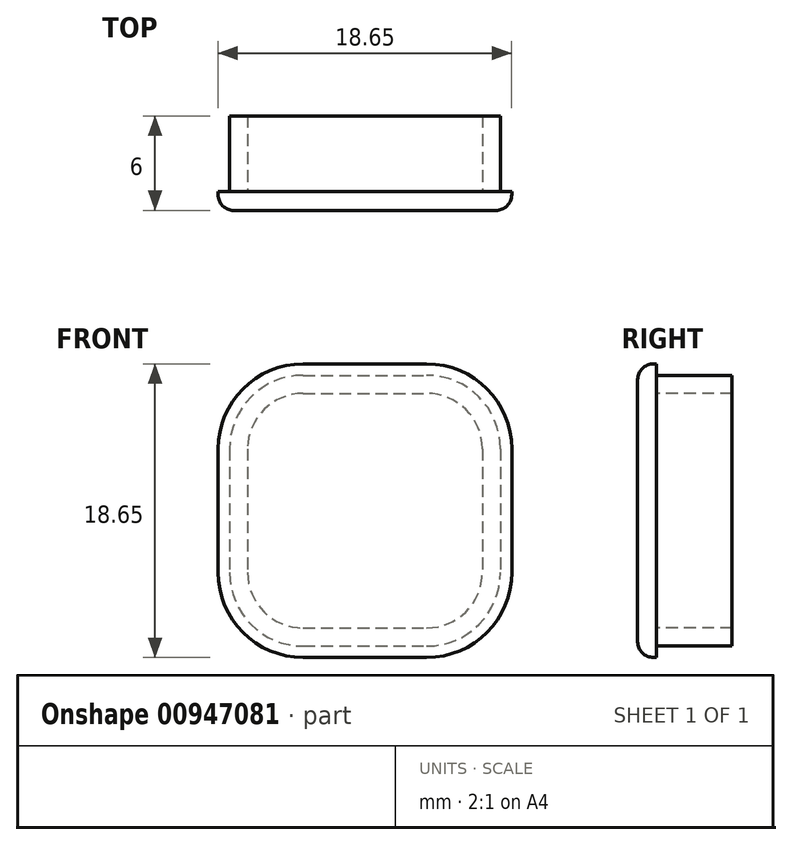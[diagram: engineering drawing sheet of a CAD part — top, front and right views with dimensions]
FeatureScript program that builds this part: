
annotation { "Feature Type Name" : "Feature", "Feature Type Description" : "" }
export const myFeature = defineFeature(function(context is Context, id is Id, definition is map)
    precondition{}
    {
        {
            var Q0;
            Q0=qCreatedBy(makeId("Front.planeOp"),FACE);
            var sketch = newSketch(context, id + "F0", { "sketchPlane" : qUnion([Q0])});
            skLineSegment(sketch, "E0.bottom", {"start": v(-49.34, 42.74) * mm, "end": v(-41.49, 42.74) * mm});
            skLineSegment(sketch, "E0.top", {"start": v(-49.34, 24.1) * mm, "end": v(-41.49, 24.1) * mm});
            skLineSegment(sketch, "E0.left", {"start": v(-54.74, 37.34) * mm, "end": v(-54.74, 29.5) * mm});
            skLineSegment(sketch, "E0.right", {"start": v(-36.09, 37.34) * mm, "end": v(-36.09, 29.5) * mm});
            skPoint(sketch, "E1.visualSharp", {"position": v(-54.74, 42.74) * mm});
            skArc(sketch, "E1.filletArc", {"start": v(-49.34, 42.74) * mm, "mid": v(-53.16, 41.16) * mm, "end": v(-54.74, 37.34) * mm});
            skPoint(sketch, "E2.visualSharp", {"position": v(-54.74, 24.1) * mm});
            skArc(sketch, "E2.filletArc", {"start": v(-54.74, 29.5) * mm, "mid": v(-53.16, 25.67) * mm, "end": v(-49.34, 24.1) * mm});
            skPoint(sketch, "E3.visualSharp", {"position": v(-36.09, 24.1) * mm});
            skArc(sketch, "E3.filletArc", {"start": v(-41.49, 24.1) * mm, "mid": v(-37.67, 25.67) * mm, "end": v(-36.09, 29.5) * mm});
            skPoint(sketch, "E4.visualSharp", {"position": v(-36.09, 42.74) * mm});
            skArc(sketch, "E4.filletArc", {"start": v(-36.09, 37.34) * mm, "mid": v(-37.67, 41.16) * mm, "end": v(-41.49, 42.74) * mm});
            skArc(sketch, "E5.0", {"start": v(-54.01, 29.5) * mm, "mid": v(-52.64, 26.19) * mm, "end": v(-49.34, 24.82) * mm});
            skLineSegment(sketch, "E5.1", {"start": v(-54.01, 37.34) * mm, "end": v(-54.01, 29.5) * mm});
            skLineSegment(sketch, "E5.2", {"start": v(-49.34, 24.82) * mm, "end": v(-41.49, 24.82) * mm});
            skArc(sketch, "E5.3", {"start": v(-49.34, 42.02) * mm, "mid": v(-52.64, 40.65) * mm, "end": v(-54.01, 37.34) * mm});
            skArc(sketch, "E5.4", {"start": v(-41.49, 24.82) * mm, "mid": v(-38.18, 26.19) * mm, "end": v(-36.81, 29.5) * mm});
            skLineSegment(sketch, "E5.5", {"start": v(-36.81, 37.34) * mm, "end": v(-36.81, 29.5) * mm});
            skArc(sketch, "E5.6", {"start": v(-36.81, 37.34) * mm, "mid": v(-38.18, 40.65) * mm, "end": v(-41.49, 42.02) * mm});
            skLineSegment(sketch, "E5.7", {"start": v(-49.34, 42.02) * mm, "end": v(-41.49, 42.02) * mm});
            skLineSegment(sketch, "E6.0", {"start": v(-52.86, 37.34) * mm, "end": v(-52.86, 29.5) * mm});
            skArc(sketch, "E6.1", {"start": v(-49.34, 40.87) * mm, "mid": v(-51.83, 39.84) * mm, "end": v(-52.86, 37.34) * mm});
            skArc(sketch, "E6.2", {"start": v(-52.86, 29.5) * mm, "mid": v(-51.83, 27) * mm, "end": v(-49.34, 25.97) * mm});
            skLineSegment(sketch, "E6.3", {"start": v(-49.34, 40.87) * mm, "end": v(-41.49, 40.87) * mm});
            skLineSegment(sketch, "E6.4", {"start": v(-49.34, 25.97) * mm, "end": v(-41.49, 25.97) * mm});
            skArc(sketch, "E6.5", {"start": v(-41.49, 25.97) * mm, "mid": v(-39, 27) * mm, "end": v(-37.96, 29.5) * mm});
            skLineSegment(sketch, "E6.6", {"start": v(-37.96, 37.34) * mm, "end": v(-37.96, 29.5) * mm});
            skArc(sketch, "E6.7", {"start": v(-37.96, 37.34) * mm, "mid": v(-39, 39.84) * mm, "end": v(-41.49, 40.87) * mm});
            skSolve(sketch);
        }
        {
            var Q0;
            Q0=makeQuery(id+"F0.imprint","IMPRINT",FACE,{"disambiguationData":[TD([[makeQuery(id+"F0.imprint","IMPRINT",EDGE,{"derivedFrom":sQuery(id+"F0.wireOp",EDGE,"E6.0")}),1.0]])]});
            var Q1;
            Q1=makeQuery(id+"F0.imprint","IMPRINT",FACE,{"disambiguationData":[TD([[makeQuery(id+"F0.imprint","IMPRINT",EDGE,{"derivedFrom":sQuery(id+"F0.wireOp",EDGE,"E5.0")}),1.0]])]});
            var Q2;
            Q2=makeQuery(id+"F0.imprint","IMPRINT",FACE,{"disambiguationData":[TD([[makeQuery(id+"F0.imprint","IMPRINT",EDGE,{"derivedFrom":sQuery(id+"F0.wireOp",EDGE,"E0.bottom")}),-1.0]])]});
            extrude(context, id + "F1", {"entities" : qUnion([Q0, Q1, Q2]), "depth" : 1.2 * mm, "offsetDistance" : 25 * mm});
        }
        {
            var Q0;
            Q0=makeQuery(id+"F0.imprint","IMPRINT",FACE,{"disambiguationData":[TD([[makeQuery(id+"F0.imprint","IMPRINT",EDGE,{"derivedFrom":sQuery(id+"F0.wireOp",EDGE,"E5.0")}),1.0]])]});
            extrude(context, id + "F2", {"entities" : qUnion([Q0]), "operationType" : NewBodyOperationType.ADD, "depth" : -4.8 * mm, "offsetDistance" : 25 * mm});
        }
        {
            var Q0;
            Q0=makeQuery(id+"F1.opExtrude","CAP_EDGE",EDGE,{"disambiguationData":[OSD([sQuery(id+"F0.wireOp",EDGE,"E4.filletArc")])],"isStart":false});
            fillet(context, id + "F3", {"entities" : qUnion([Q0]), "radius" : 1 * mm, "tangentPropagation" : true, "allowEdgeOverflow" : false});
        }
    });
